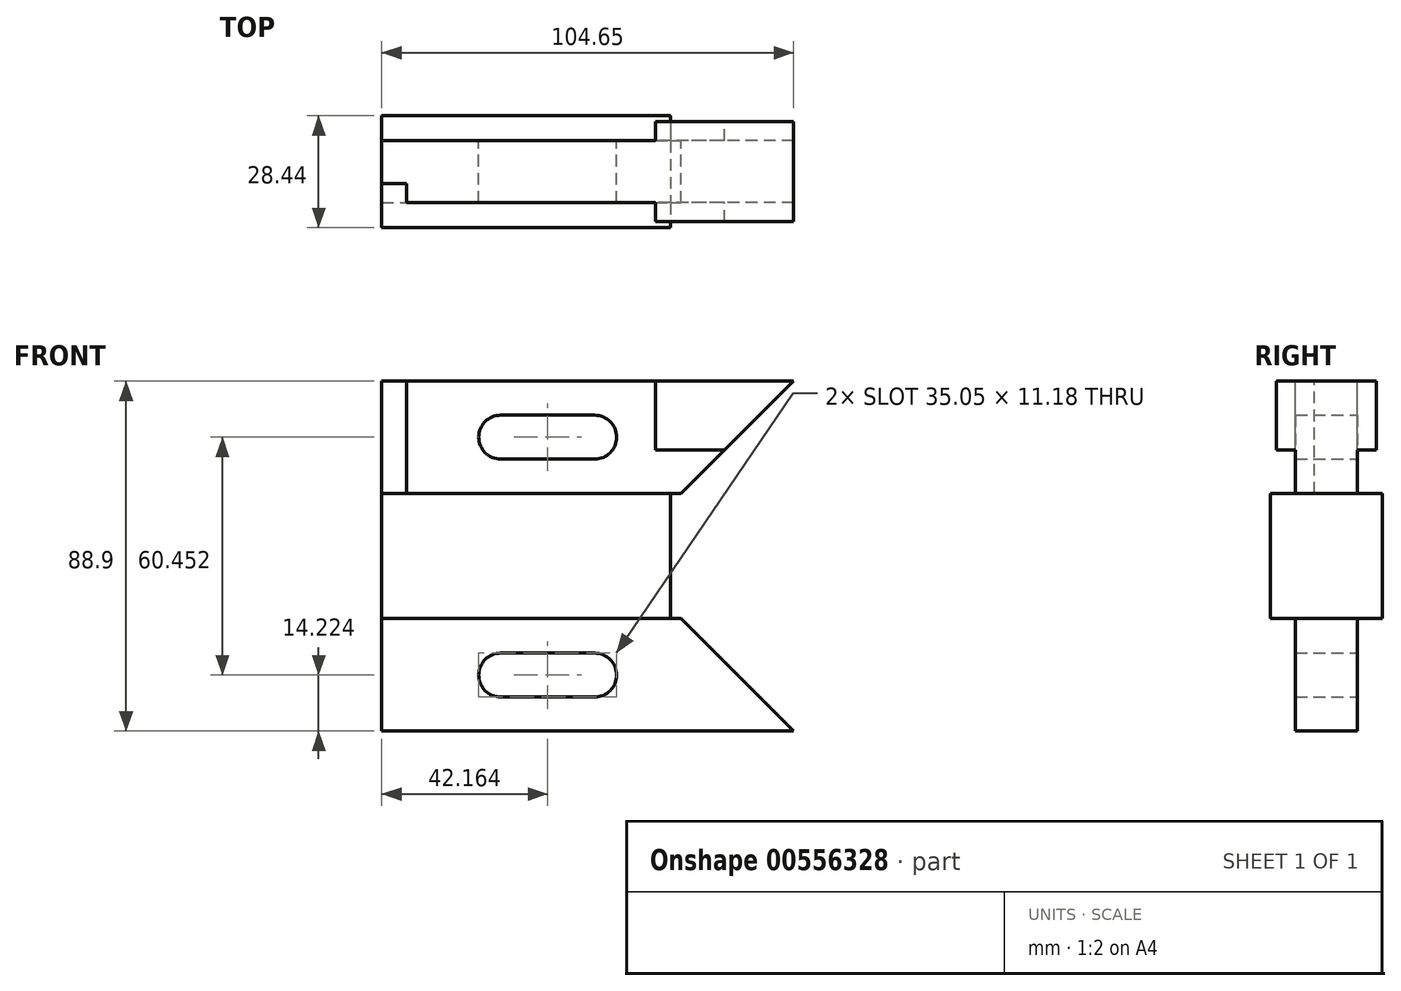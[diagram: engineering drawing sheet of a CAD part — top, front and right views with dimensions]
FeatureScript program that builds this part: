
annotation { "Feature Type Name" : "Feature", "Feature Type Description" : "" }
export const myFeature = defineFeature(function(context is Context, id is Id, definition is map)
    precondition{}
    {
        {
            var Q0;
            Q0=qCreatedBy(makeId("Right.planeOp"),FACE);
            var sketch = newSketch(context, id + "F0", { "sketchPlane" : qUnion([Q0])});
            skLineSegment(sketch, "E0.bottom", {"start": v(14.22, 15.88) * mm, "end": v(-14.22, 15.87) * mm});
            skLineSegment(sketch, "E0.top", {"start": v(14.22, -15.87) * mm, "end": v(-14.22, -15.88) * mm});
            skLineSegment(sketch, "E0.left", {"start": v(14.22, 15.88) * mm, "end": v(14.22, -15.88) * mm});
            skLineSegment(sketch, "E0.right", {"start": v(-14.22, 15.87) * mm, "end": v(-14.22, -15.88) * mm});
            skPoint(sketch, "E0.middle", {"position": v(0, 0) * mm});
            skSolve(sketch);
        }
        {
            var Q0;
            Q0=makeQuery(id+"F0.imprint","IMPRINT",FACE,{"disambiguationData":[TD([[makeQuery(id+"F0.imprint","IMPRINT",EDGE,{"derivedFrom":sQuery(id+"F0.wireOp",EDGE,"E0.bottom")}),1.0]])]});
            var Q1;
            Q1 = qSketchRegion(id + "F6", true);
            extrude(context, id + "F1", {"entities" : qUnion([Q0, Q1]), "depth" : 73.4 * mm, "offsetDistance" : 25.4 * mm});
        }
        {
            var Q0;
            Q0=qCreatedBy(makeId("Front.planeOp"),FACE);
            var sketch = newSketch(context, id + "F2", { "sketchPlane" : qUnion([Q0])});
            skLineSegment(sketch, "E1.0.1", {"start": v(0, 15.87) * mm, "end": v(73.4, 15.87) * mm});
            skLineSegment(sketch, "E1.0.3", {"start": v(73.4, 15.88) * mm, "end": v(0, 15.88) * mm});
            skLineSegment(sketch, "E2", {"start": v(0, 15.87) * mm, "end": v(0, 44.45) * mm});
            skLineSegment(sketch, "E3", {"start": v(0, 44.45) * mm, "end": v(104.65, 44.45) * mm});
            skLineSegment(sketch, "E4", {"start": v(104.65, 44.45) * mm, "end": v(76.07, 15.87) * mm});
            skLineSegment(sketch, "E5", {"start": v(76.07, 15.87) * mm, "end": v(73.4, 15.87) * mm});
            skCircle(sketch, "E6", {"center": v(30.23, 30.23) * mm, "radius": 5.59 * mm});
            skCircle(sketch, "E7", {"center": v(54.1, 30.23) * mm, "radius": 5.59 * mm});
            skLineSegment(sketch, "E8", {"start": v(30.23, 35.81) * mm, "end": v(54.1, 35.81) * mm});
            skLineSegment(sketch, "E9", {"start": v(30.23, 24.64) * mm, "end": v(54.1, 24.64) * mm});
            skLineSegment(sketch, "E10.MirrorCS", {"start": v(76.07, -15.87) * mm, "end": v(73.4, -15.87) * mm});
            skLineSegment(sketch, "E11.MirrorCS", {"start": v(0, -15.87) * mm, "end": v(73.4, -15.87) * mm});
            skLineSegment(sketch, "E12.MirrorCS", {"start": v(0, -44.45) * mm, "end": v(104.65, -44.45) * mm});
            skCircle(sketch, "E13.MirrorC", {"center": v(54.1, -30.23) * mm, "radius": 5.59 * mm});
            skLineSegment(sketch, "E14.MirrorCS", {"start": v(0, -15.87) * mm, "end": v(0, -44.45) * mm});
            skLineSegment(sketch, "E15.MirrorCS", {"start": v(104.65, -44.45) * mm, "end": v(76.07, -15.87) * mm});
            skLineSegment(sketch, "E16.MirrorCS", {"start": v(30.23, -24.64) * mm, "end": v(54.1, -24.64) * mm});
            skCircle(sketch, "E17.MirrorC", {"center": v(30.23, -30.23) * mm, "radius": 5.59 * mm});
            skLineSegment(sketch, "E18.MirrorCS", {"start": v(30.23, -35.81) * mm, "end": v(54.1, -35.81) * mm});
            skLineSegment(sketch, "E19.MirrorCS", {"start": v(73.4, -15.88) * mm, "end": v(0, -15.88) * mm});
            skSolve(sketch);
        }
        {
            var Q0;
            Q0 = qSketchRegion(id + "F2", true);
            extrude(context, id + "F3", {"entities" : qUnion([Q0]), "operationType" : NewBodyOperationType.ADD, "endBound" : BoundingType.SYMMETRIC, "depth" : 15.75 * mm, "offsetDistance" : 25.4 * mm});
        }
        {
            var Q0;
            Q0=makeQuery(id+"F3.opExtrude","CAP_FACE",FACE,{"disambiguationData":[OSD([sQuery(id+"F2.wireOp",EDGE,"E1.0.3"),sQuery(id+"F2.wireOp",EDGE,"E2"),sQuery(id+"F2.wireOp",EDGE,"E3"),sQuery(id+"F2.wireOp",EDGE,"E4"),sQuery(id+"F2.wireOp",EDGE,"E5"),sQuery(id+"F2.wireOp",EDGE,"E6"),sQuery(id+"F2.wireOp",EDGE,"E7"),sQuery(id+"F2.wireOp",EDGE,"E8"),sQuery(id+"F2.wireOp",EDGE,"E9")])],"isStart":false});
            var sketch = newSketch(context, id + "F4", { "sketchPlane" : qUnion([Q0])});
            skLineSegment(sketch, "E20.bottom", {"start": v(0, 15.87) * mm, "end": v(6.35, 15.87) * mm});
            skLineSegment(sketch, "E20.top", {"start": v(0, 44.45) * mm, "end": v(6.35, 44.45) * mm});
            skLineSegment(sketch, "E20.left", {"start": v(0, 15.87) * mm, "end": v(0, 44.45) * mm});
            skLineSegment(sketch, "E20.right", {"start": v(6.35, 15.87) * mm, "end": v(6.35, 44.45) * mm});
            skSolve(sketch);
        }
        {
            var Q0;
            Q0 = qSketchRegion(id + "F4", true);
            extrude(context, id + "F5", {"entities" : qUnion([Q0]), "operationType" : NewBodyOperationType.REMOVE, "oppositeDirection" : true, "depth" : 4.83 * mm, "offsetDistance" : 25.4 * mm});
        }
        {
            var Q0;
            Q0=qCreatedBy(makeId("Front.planeOp"),FACE);
            var sketch = newSketch(context, id + "F6", { "sketchPlane" : qUnion([Q0])});
            skLineSegment(sketch, "E21.0", {"start": v(6.35, 44.45) * mm, "end": v(104.65, 44.45) * mm});
            skLineSegment(sketch, "E22.0", {"start": v(104.65, 44.45) * mm, "end": v(76.07, 15.87) * mm});
            skLineSegment(sketch, "E23", {"start": v(69.6, 44.45) * mm, "end": v(69.6, 26.92) * mm});
            skLineSegment(sketch, "E24", {"start": v(69.6, 26.92) * mm, "end": v(87.12, 26.92) * mm});
            skSolve(sketch);
        }
        {
            var Q0;
            Q0 = qSketchRegion(id + "F6", true);
            extrude(context, id + "F7", {"entities" : qUnion([Q0]), "operationType" : NewBodyOperationType.ADD, "endBound" : BoundingType.SYMMETRIC, "depth" : 25.4 * mm, "offsetDistance" : 25.4 * mm});
        }
    });
